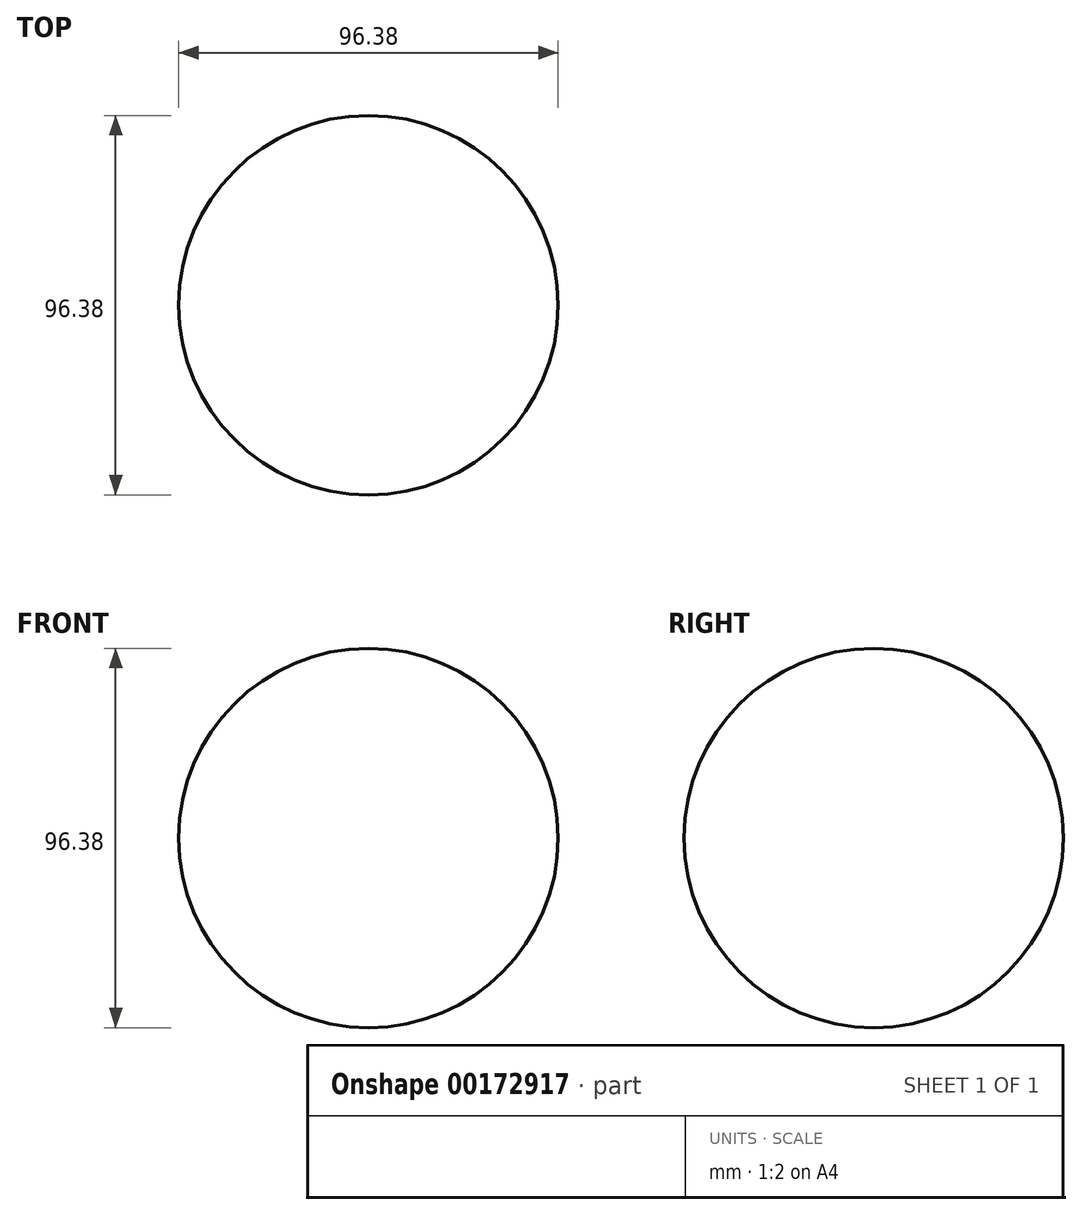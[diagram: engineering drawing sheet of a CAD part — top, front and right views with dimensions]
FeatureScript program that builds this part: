
annotation { "Feature Type Name" : "Feature", "Feature Type Description" : "" }
export const myFeature = defineFeature(function(context is Context, id is Id, definition is map)
    precondition{}
    {
        {
            var Q0;
            Q0=qCreatedBy(makeId("Top.planeOp"),FACE);
            var sketch = newSketch(context, id + "F0", { "sketchPlane" : qUnion([Q0])});
            skArc(sketch, "E0", {"start": v(48.19, 0) * mm, "mid": v(0, 48.19) * mm, "end": v(-48.19, 0) * mm});
            skLineSegment(sketch, "E1", {"start": v(-48.19, 0) * mm, "end": v(48.19, 0) * mm});
            skSolve(sketch);
        }
        {
            var Q0;
            Q0=makeQuery(id+"F0.imprint","IMPRINT",FACE,{"disambiguationData":[TD([[makeQuery(id+"F0.imprint","IMPRINT",EDGE,{"derivedFrom":sQuery(id+"F0.wireOp",EDGE,"E0")}),1.0]])]});
            var Q1;
            Q1=sQuery(id+"F0.wireOp",EDGE,"E1");
            revolve(context, id + "F1", {"entities" : qUnion([Q0]), "axis" : qUnion([Q1]), "revolveType" : RevolveType.FULL});
        }
    });
